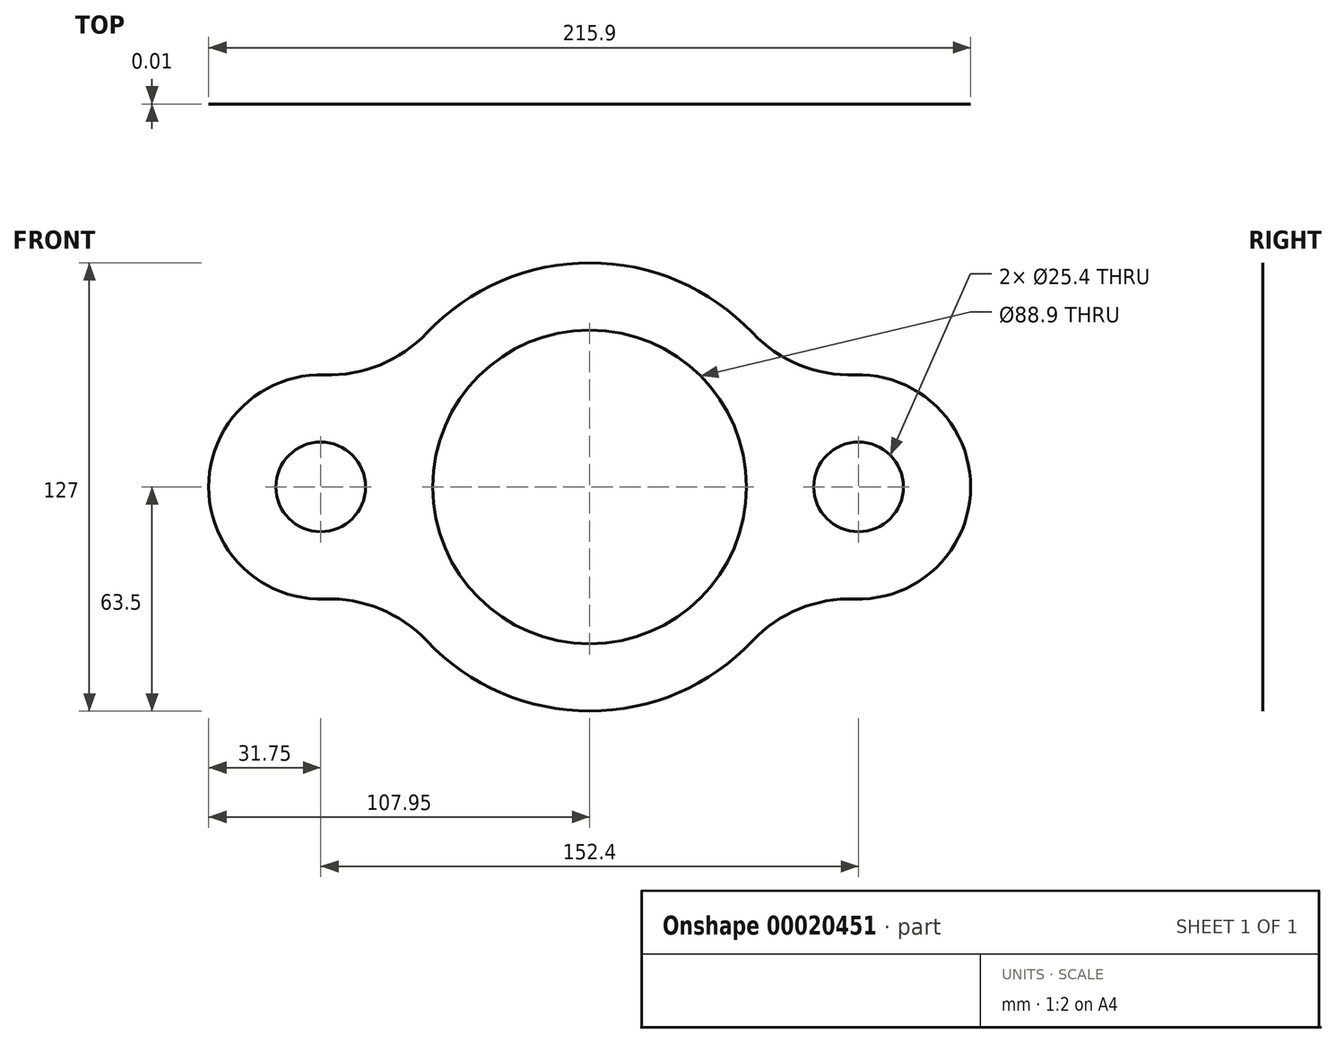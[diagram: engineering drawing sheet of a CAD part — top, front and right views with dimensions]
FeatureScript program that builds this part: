
annotation { "Feature Type Name" : "Feature", "Feature Type Description" : "" }
export const myFeature = defineFeature(function(context is Context, id is Id, definition is map)
    precondition{}
    {
        {
            var Q0;
            Q0=qCreatedBy(makeId("Front.planeOp"),FACE);
            var sketch = newSketch(context, id + "F0", { "sketchPlane" : qUnion([Q0])});
            skCircle(sketch, "E0", {"center": v(0, 0) * mm, "radius": 44.45 * mm});
            skCircle(sketch, "E1", {"center": v(-76.2, 0) * mm, "radius": 12.7 * mm});
            skCircle(sketch, "E2", {"center": v(76.2, 0) * mm, "radius": 12.7 * mm});
            skArc(sketch, "E3", {"start": v(46.14, 43.63) * mm, "mid": v(0, 63.5) * mm, "end": v(-46.14, 43.63) * mm});
            skArc(sketch, "E4", {"start": v(-75.12, 31.73) * mm, "mid": v(-107.95, 0) * mm, "end": v(-75.12, -31.73) * mm});
            skArc(sketch, "E5", {"start": v(75.12, -31.73) * mm, "mid": v(107.95, 0) * mm, "end": v(75.12, 31.73) * mm});
            skArc(sketch, "E6.trimOffspring", {"start": v(-46.14, -43.63) * mm, "mid": v(0, -63.5) * mm, "end": v(46.14, -43.63) * mm});
            skPoint(sketch, "E7.visualSharp", {"position": v(-57.94, -25.98) * mm});
            skArc(sketch, "E7.filletArc", {"start": v(-46.14, -43.63) * mm, "mid": v(-59.35, -34.56) * mm, "end": v(-75.12, -31.73) * mm});
            skPoint(sketch, "E8.visualSharp", {"position": v(-57.94, 25.98) * mm});
            skArc(sketch, "E8.filletArc", {"start": v(-75.12, 31.73) * mm, "mid": v(-59.35, 34.56) * mm, "end": v(-46.14, 43.63) * mm});
            skPoint(sketch, "E9.visualSharp", {"position": v(57.94, 25.98) * mm});
            skArc(sketch, "E9.filletArc", {"start": v(46.14, 43.63) * mm, "mid": v(59.35, 34.56) * mm, "end": v(75.12, 31.73) * mm});
            skPoint(sketch, "E10.visualSharp", {"position": v(57.94, -25.98) * mm});
            skArc(sketch, "E10.filletArc", {"start": v(75.12, -31.73) * mm, "mid": v(59.35, -34.56) * mm, "end": v(46.14, -43.63) * mm});
            skSolve(sketch);
        }
        {
            var Q0;
            Q0=makeQuery(id+"F0.imprint","IMPRINT",FACE,{"disambiguationData":[TD([[makeQuery(id+"F0.imprint","IMPRINT",EDGE,{"derivedFrom":sQuery(id+"F0.wireOp",EDGE,"E0")}),-1.0]])]});
            extrude(context, id + "F1", {"entities" : qUnion([Q0]), "oppositeDirection" : true, "depth" : 1 / 101.6 * mm});
        }
    });
